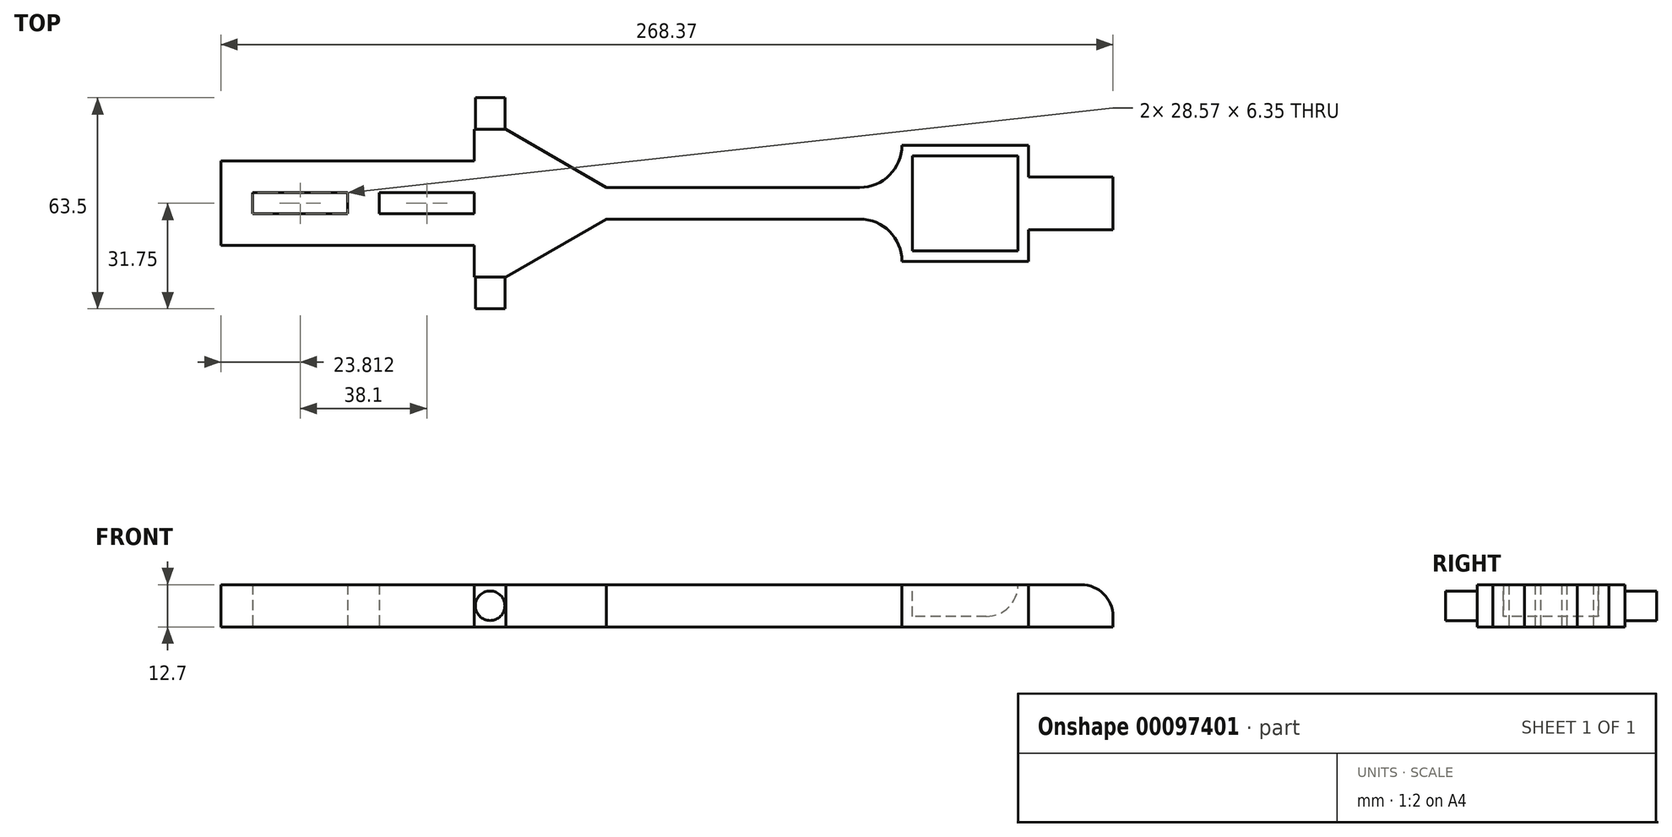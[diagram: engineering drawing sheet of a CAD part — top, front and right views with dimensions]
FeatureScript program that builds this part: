
annotation { "Feature Type Name" : "Feature", "Feature Type Description" : "" }
export const myFeature = defineFeature(function(context is Context, id is Id, definition is map)
    precondition{}
    {
        {
            var Q0;
            Q0=qCreatedBy(makeId("Top.planeOp"),FACE);
            var sketch = newSketch(context, id + "F0", { "sketchPlane" : qUnion([Q0])});
            skLineSegment(sketch, "E0.bottom", {"start": v(0, -12.7) * mm, "end": v(-76.2, -12.7) * mm});
            skLineSegment(sketch, "E0.top", {"start": v(0, 12.7) * mm, "end": v(-76.2, 12.7) * mm});
            skLineSegment(sketch, "E0.left", {"start": v(0, -3.17) * mm, "end": v(0, 3.17) * mm});
            skLineSegment(sketch, "E0.right", {"start": v(-76.2, -12.7) * mm, "end": v(-76.2, 12.7) * mm});
            skLineSegment(sketch, "E1.bottom", {"start": v(0, -3.17) * mm, "end": v(-28.58, -3.17) * mm});
            skLineSegment(sketch, "E1.top", {"start": v(0, 3.17) * mm, "end": v(-28.58, 3.17) * mm});
            skLineSegment(sketch, "E1.right", {"start": v(-28.58, -3.17) * mm, "end": v(-28.58, 3.17) * mm});
            skLineSegment(sketch, "E2.bottom", {"start": v(-66.68, 3.17) * mm, "end": v(-38.1, 3.17) * mm});
            skLineSegment(sketch, "E2.top", {"start": v(-66.68, -3.17) * mm, "end": v(-38.1, -3.17) * mm});
            skLineSegment(sketch, "E2.left", {"start": v(-66.68, 3.18) * mm, "end": v(-66.68, -3.18) * mm});
            skLineSegment(sketch, "E2.right", {"start": v(-38.1, 3.18) * mm, "end": v(-38.1, -3.18) * mm});
            skLineSegment(sketch, "E3", {"start": v(-76.2, 0) * mm, "end": v(-66.68, 0) * mm, "construction": true});
            skLineSegment(sketch, "E4", {"start": v(-52.39, 12.7) * mm, "end": v(-52.39, 3.18) * mm, "construction": true});
            skLineSegment(sketch, "E5", {"start": v(-38.1, 0) * mm, "end": v(-28.58, 0) * mm, "construction": true});
            skPoint(sketch, "E5.startSnap0", {"position": v(-38.1, 0) * mm});
            skLineSegment(sketch, "E6", {"start": v(-14.29, 3.17) * mm, "end": v(-14.29, 12.7) * mm, "construction": true});
            skLineSegment(sketch, "E7.bottom", {"start": v(0, 22.23) * mm, "end": v(9.53, 22.23) * mm});
            skLineSegment(sketch, "E7.top", {"start": v(0, -22.23) * mm, "end": v(9.53, -22.23) * mm});
            skLineSegment(sketch, "E7.left", {"start": v(0, 22.23) * mm, "end": v(0, 12.7) * mm});
            skLineSegment(sketch, "E7.right", {"start": v(9.53, 22.22) * mm, "end": v(9.53, -22.22) * mm, "construction": true});
            skLineSegment(sketch, "E8", {"start": v(-52.39, -3.18) * mm, "end": v(-52.39, -12.7) * mm, "construction": true});
            skLineSegment(sketch, "E9.trimOffspring", {"start": v(0, 3.18) * mm, "end": v(0, -3.17) * mm});
            skLineSegment(sketch, "E10.trimOffspring", {"start": v(0, -12.7) * mm, "end": v(0, -22.23) * mm});
            skPoint(sketch, "E11.endSnap0", {"position": v(9.52, 0) * mm});
            skLineSegment(sketch, "E12", {"start": v(9.52, 22.23) * mm, "end": v(39.77, 4.76) * mm});
            skLineSegment(sketch, "E13", {"start": v(39.77, -4.76) * mm, "end": v(9.52, -22.23) * mm});
            skLineSegment(sketch, "E14.bottom", {"start": v(39.77, 4.76) * mm, "end": v(115.97, 4.76) * mm});
            skLineSegment(sketch, "E14.top", {"start": v(39.77, -4.76) * mm, "end": v(115.97, -4.76) * mm});
            skLineSegment(sketch, "E14.left", {"start": v(39.77, 4.76) * mm, "end": v(39.77, -4.76) * mm, "construction": true});
            skArc(sketch, "E15", {"start": v(115.97, 4.76) * mm, "mid": v(124.95, 8.48) * mm, "end": v(128.67, 17.46) * mm});
            skArc(sketch, "E16", {"start": v(128.67, -17.46) * mm, "mid": v(124.95, -8.48) * mm, "end": v(115.97, -4.76) * mm});
            skLineSegment(sketch, "E17.bottom", {"start": v(128.67, 17.46) * mm, "end": v(166.77, 17.46) * mm});
            skLineSegment(sketch, "E17.top", {"start": v(128.67, -17.46) * mm, "end": v(166.77, -17.46) * mm});
            skLineSegment(sketch, "E17.right", {"start": v(166.77, 17.46) * mm, "end": v(166.77, 7.94) * mm});
            skLineSegment(sketch, "E18.bottom", {"start": v(166.77, 7.94) * mm, "end": v(192.17, 7.94) * mm});
            skLineSegment(sketch, "E18.top", {"start": v(166.77, -7.94) * mm, "end": v(192.17, -7.94) * mm});
            skLineSegment(sketch, "E18.right", {"start": v(192.17, 7.94) * mm, "end": v(192.17, -7.94) * mm});
            skLineSegment(sketch, "E19.trimOffspring", {"start": v(166.77, -7.94) * mm, "end": v(166.77, -17.46) * mm});
            skLineSegment(sketch, "E20", {"start": v(9.52, 0) * mm, "end": v(39.77, 0) * mm, "construction": true});
            skSolve(sketch);
        }
        {
            var Q0;
            Q0=makeQuery(id+"F0.imprint","IMPRINT",FACE,{"disambiguationData":[TD([[makeQuery(id+"F0.imprint","IMPRINT",EDGE,{"derivedFrom":sQuery(id+"F0.wireOp",EDGE,"E0.bottom")}),-1.0]])]});
            extrude(context, id + "F1", {"entities" : qUnion([Q0]), "depth" : 12.7 * mm});
        }
        {
            var Q0;
            Q0=makeQuery(id+"F1.opExtrude","SWEPT_FACE",FACE,{"disambiguationData":[OSD([sQuery(id+"F0.wireOp",EDGE,"E7.top")])]});
            var sketch = newSketch(context, id + "F2", { "sketchPlane" : qUnion([Q0])});
            skCircle(sketch, "E21", {"center": v(4.76, 6.35) * mm, "radius": 4.45 * mm});
            skPoint(sketch, "E21.centerSnap0", {"position": v(4.76, 12.7) * mm});
            skLineSegment(sketch, "E22", {"start": v(0, 12.7) * mm, "end": v(9.52, 0) * mm, "construction": true});
            skSolve(sketch);
        }
        {
            var Q0;
            Q0=makeQuery(id+"F2.imprint","IMPRINT",FACE,{"disambiguationData":[TD([[makeQuery(id+"F2.imprint","IMPRINT",EDGE,{"derivedFrom":sQuery(id+"F2.wireOp",EDGE,"E21")}),1.0]])]});
            extrude(context, id + "F3", {"entities" : qUnion([Q0]), "operationType" : NewBodyOperationType.ADD, "depth" : 9.52 * mm});
        }
        {
            var Q0;
            Q0=makeQuery(id+"F1.opExtrude","SWEPT_FACE",FACE,{"disambiguationData":[OSD([sQuery(id+"F0.wireOp",EDGE,"E7.bottom")])]});
            var sketch = newSketch(context, id + "F4", { "sketchPlane" : qUnion([Q0])});
            skCircle(sketch, "E23.0", {"center": v(-4.76, 6.35) * mm, "radius": 4.45 * mm});
            skSolve(sketch);
        }
        {
            var Q0;
            Q0=qSketchRegion(id+"F4",true);
            extrude(context, id + "F5", {"entities" : qUnion([Q0]), "operationType" : NewBodyOperationType.ADD, "depth" : 9.52 * mm});
        }
        {
            var Q0;
            Q0=makeQuery(id+"F1.opExtrude","CAP_FACE",FACE,{"disambiguationData":[OSD([sQuery(id+"F0.wireOp",EDGE,"E0.bottom"),sQuery(id+"F0.wireOp",EDGE,"E0.top"),sQuery(id+"F0.wireOp",EDGE,"E0.right"),sQuery(id+"F0.wireOp",EDGE,"E1.bottom"),sQuery(id+"F0.wireOp",EDGE,"E1.top"),sQuery(id+"F0.wireOp",EDGE,"E1.right"),sQuery(id+"F0.wireOp",EDGE,"E2.bottom"),sQuery(id+"F0.wireOp",EDGE,"E2.top"),sQuery(id+"F0.wireOp",EDGE,"E2.left"),sQuery(id+"F0.wireOp",EDGE,"E2.right"),sQuery(id+"F0.wireOp",EDGE,"E7.bottom"),sQuery(id+"F0.wireOp",EDGE,"E7.top"),sQuery(id+"F0.wireOp",EDGE,"E7.left"),sQuery(id+"F0.wireOp",EDGE,"E9.trimOffspring"),sQuery(id+"F0.wireOp",EDGE,"E10.trimOffspring"),sQuery(id+"F0.wireOp",EDGE,"E12"),sQuery(id+"F0.wireOp",EDGE,"E13"),sQuery(id+"F0.wireOp",EDGE,"E14.bottom"),sQuery(id+"F0.wireOp",EDGE,"E14.top"),sQuery(id+"F0.wireOp",EDGE,"E15"),sQuery(id+"F0.wireOp",EDGE,"E16"),sQuery(id+"F0.wireOp",EDGE,"E17.bottom"),sQuery(id+"F0.wireOp",EDGE,"E17.top"),sQuery(id+"F0.wireOp",EDGE,"E17.right"),sQuery(id+"F0.wireOp",EDGE,"E18.bottom"),sQuery(id+"F0.wireOp",EDGE,"E18.top"),sQuery(id+"F0.wireOp",EDGE,"E18.right"),sQuery(id+"F0.wireOp",EDGE,"E19.trimOffspring")])],"isStart":false});
            var sketch = newSketch(context, id + "F6", { "sketchPlane" : qUnion([Q0])});
            skLineSegment(sketch, "E24.bottom", {"start": v(163.6, 14.29) * mm, "end": v(131.85, 14.29) * mm});
            skLineSegment(sketch, "E24.top", {"start": v(163.6, -14.29) * mm, "end": v(131.85, -14.29) * mm});
            skLineSegment(sketch, "E24.left", {"start": v(163.6, 14.29) * mm, "end": v(163.6, -14.29) * mm});
            skLineSegment(sketch, "E24.right", {"start": v(131.85, 14.29) * mm, "end": v(131.85, -14.29) * mm});
            skPoint(sketch, "E24.middle", {"position": v(147.72, 0) * mm});
            skLineSegment(sketch, "E25", {"start": v(147.72, 17.46) * mm, "end": v(147.72, 14.29) * mm, "construction": true});
            skLineSegment(sketch, "E26", {"start": v(166.77, -7.94) * mm, "end": v(163.6, -7.94) * mm, "construction": true});
            skLineSegment(sketch, "E27", {"start": v(128.67, 17.46) * mm, "end": v(166.77, -17.46) * mm, "construction": true});
            skSolve(sketch);
        }
        {
            var Q0;
            Q0=makeQuery(id+"F6.imprint","IMPRINT",FACE,{"disambiguationData":[TD([[makeQuery(id+"F6.imprint","IMPRINT",EDGE,{"derivedFrom":sQuery(id+"F6.wireOp",EDGE,"E24.bottom")}),1.0]])]});
            extrude(context, id + "F7", {"entities" : qUnion([Q0]), "operationType" : NewBodyOperationType.REMOVE, "oppositeDirection" : true, "depth" : 9.52 * mm});
        }
        {
            var Q0;
            Q0=makeQuery(id+"F7.boolean.opBoolean","COPY",EDGE,{"derivedFrom":makeQuery(id+"F7.opExtrude","CAP_EDGE",EDGE,{"disambiguationData":[OSD([sQuery(id+"F6.wireOp",EDGE,"E24.left")])],"isStart":false})});
            var Q1;
            Q1=makeQuery(id+"F1.opExtrude","CAP_EDGE",EDGE,{"disambiguationData":[OSD([sQuery(id+"F0.wireOp",EDGE,"E18.right")])],"isStart":false});
            fillet(context, id + "F8", {"entities" : qUnion([Q0, Q1]), "radius" : 9.52 * mm, "tangentPropagation" : true, "allowEdgeOverflow" : false});
        }
    });
